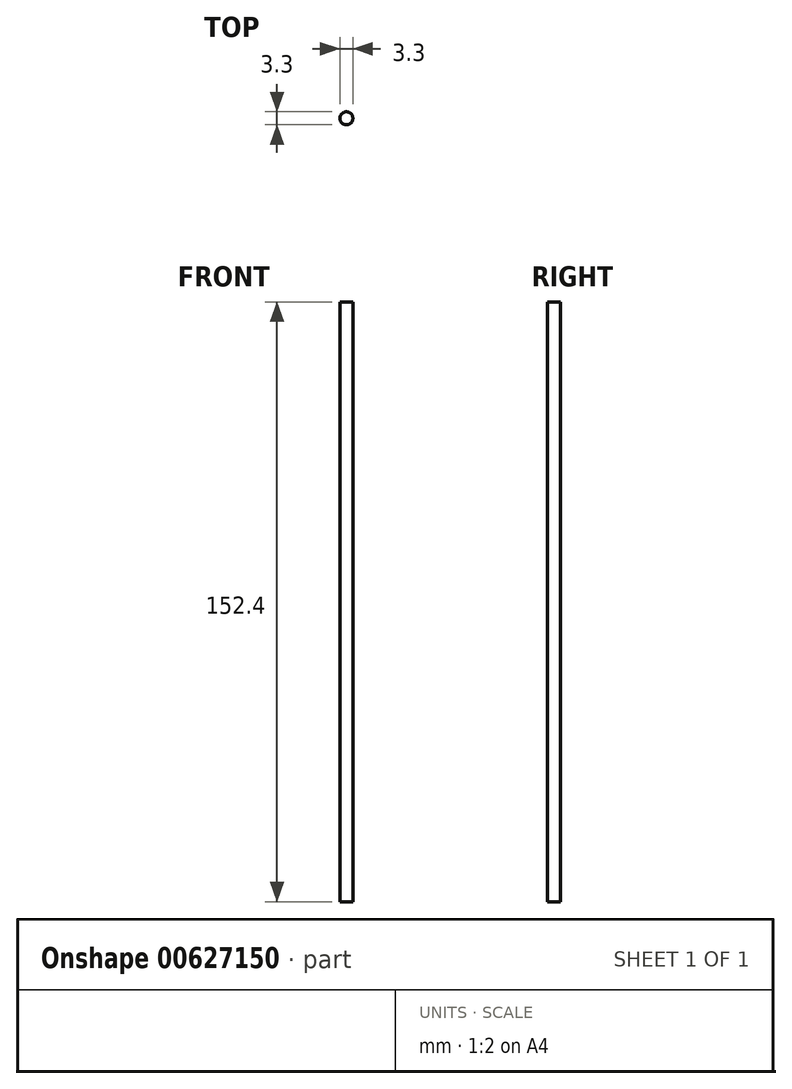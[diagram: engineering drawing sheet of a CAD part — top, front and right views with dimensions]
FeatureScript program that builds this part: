
annotation { "Feature Type Name" : "Feature", "Feature Type Description" : "" }
export const myFeature = defineFeature(function(context is Context, id is Id, definition is map)
    precondition{}
    {
        {
            var Q0;
            Q0=qCreatedBy(makeId("Top.planeOp"),FACE);
            var sketch = newSketch(context, id + "F0", { "sketchPlane" : qUnion([Q0])});
            skCircle(sketch, "E0", {"center": v(0, 0) * mm, "radius": 1.65 * mm});
            skSolve(sketch);
        }
        {
            var Q0;
            Q0 = qSketchRegion(id + "F0", true);
            extrude(context, id + "F1", {"entities" : qUnion([Q0]), "depth" : 152.4 * mm, "offsetDistance" : 25.4 * mm});
        }
    });
